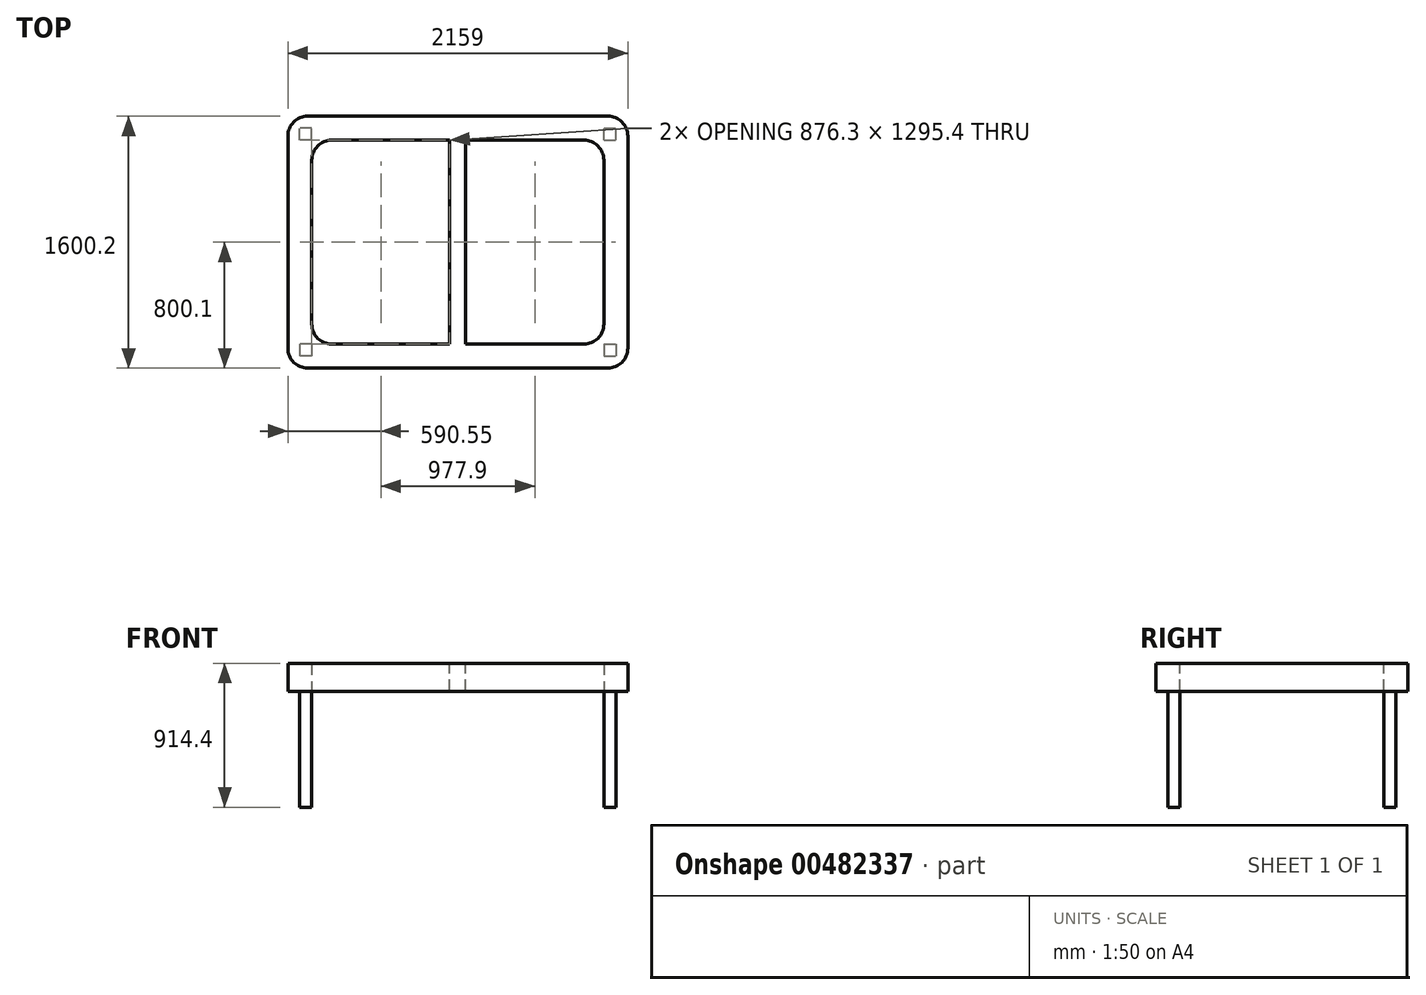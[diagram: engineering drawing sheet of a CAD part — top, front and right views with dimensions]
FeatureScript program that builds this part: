
annotation { "Feature Type Name" : "Feature", "Feature Type Description" : "" }
export const myFeature = defineFeature(function(context is Context, id is Id, definition is map)
    precondition{}
    {
        {
            var Q0;
            Q0=qCreatedBy(makeId("Top.planeOp"),FACE);
            var sketch = newSketch(context, id + "F0", { "sketchPlane" : qUnion([Q0])});
            skLineSegment(sketch, "E0.bottom", {"start": v(0, 0) * mm, "end": v(2159, 0) * mm});
            skLineSegment(sketch, "E0.top", {"start": v(0, 1600.2) * mm, "end": v(2159, 1600.2) * mm});
            skLineSegment(sketch, "E0.left", {"start": v(0, 0) * mm, "end": v(0, 1600.2) * mm});
            skLineSegment(sketch, "E0.right", {"start": v(2159, 0) * mm, "end": v(2159, 1600.2) * mm});
            skLineSegment(sketch, "E1.bottom", {"start": v(152.4, 152.4) * mm, "end": v(2006.6, 152.4) * mm});
            skLineSegment(sketch, "E1.top", {"start": v(152.4, 1447.8) * mm, "end": v(2006.6, 1447.8) * mm});
            skLineSegment(sketch, "E1.left", {"start": v(152.4, 152.4) * mm, "end": v(152.4, 1447.8) * mm});
            skLineSegment(sketch, "E1.right", {"start": v(2006.6, 152.4) * mm, "end": v(2006.6, 1447.8) * mm});
            skSolve(sketch);
        }
        {
            var Q0;
            Q0 = qSketchRegion(id + "F0", true);
            extrude(context, id + "F1", {"entities" : qUnion([Q0]), "depth" : 177.8 * mm, "offsetDistance" : 25.4 * mm});
        }
        {
            var Q0;
            Q0=makeQuery(id+"F1.opExtrude","CAP_FACE",FACE,{"disambiguationData":[OSD([sQuery(id+"F0.wireOp",EDGE,"E0.bottom"),sQuery(id+"F0.wireOp",EDGE,"E0.top"),sQuery(id+"F0.wireOp",EDGE,"E0.left"),sQuery(id+"F0.wireOp",EDGE,"E0.right"),sQuery(id+"F0.wireOp",EDGE,"E1.bottom"),sQuery(id+"F0.wireOp",EDGE,"E1.top"),sQuery(id+"F0.wireOp",EDGE,"E1.left"),sQuery(id+"F0.wireOp",EDGE,"E1.right")])],"isStart":true});
            var sketch = newSketch(context, id + "F2", { "sketchPlane" : qUnion([Q0])});
            skLineSegment(sketch, "E2.bottom", {"start": v(152.4, -152.4) * mm, "end": v(76.2, -152.4) * mm});
            skLineSegment(sketch, "E2.top", {"start": v(152.4, -76.2) * mm, "end": v(76.2, -76.2) * mm});
            skLineSegment(sketch, "E2.left", {"start": v(152.4, -152.4) * mm, "end": v(152.4, -76.2) * mm});
            skLineSegment(sketch, "E2.right", {"start": v(76.2, -152.4) * mm, "end": v(76.2, -76.2) * mm});
            skLineSegment(sketch, "E3.bottom", {"start": v(2006.6, -152.4) * mm, "end": v(2082.8, -152.4) * mm});
            skLineSegment(sketch, "E3.top", {"start": v(2006.6, -76.2) * mm, "end": v(2082.8, -76.2) * mm});
            skLineSegment(sketch, "E3.left", {"start": v(2006.6, -152.4) * mm, "end": v(2006.6, -76.2) * mm});
            skLineSegment(sketch, "E3.right", {"start": v(2082.8, -152.4) * mm, "end": v(2082.8, -76.2) * mm});
            skLineSegment(sketch, "E4.bottom", {"start": v(2006.6, -1447.8) * mm, "end": v(2082.8, -1447.8) * mm});
            skLineSegment(sketch, "E4.top", {"start": v(2006.6, -1524) * mm, "end": v(2082.8, -1524) * mm});
            skLineSegment(sketch, "E4.left", {"start": v(2006.6, -1447.8) * mm, "end": v(2006.6, -1524) * mm});
            skLineSegment(sketch, "E4.right", {"start": v(2082.8, -1447.8) * mm, "end": v(2082.8, -1524) * mm});
            skLineSegment(sketch, "E5.bottom", {"start": v(152.4, -1447.8) * mm, "end": v(76.2, -1447.8) * mm});
            skLineSegment(sketch, "E5.top", {"start": v(152.4, -1524) * mm, "end": v(76.2, -1524) * mm});
            skLineSegment(sketch, "E5.left", {"start": v(152.4, -1447.8) * mm, "end": v(152.4, -1524) * mm});
            skLineSegment(sketch, "E5.right", {"start": v(76.2, -1447.8) * mm, "end": v(76.2, -1524) * mm});
            skSolve(sketch);
        }
        {
            var Q0;
            Q0 = qSketchRegion(id + "F2", true);
            extrude(context, id + "F3", {"entities" : qUnion([Q0]), "operationType" : NewBodyOperationType.ADD, "depth" : 736.6 * mm, "offsetDistance" : 25.4 * mm});
        }
        {
            var Q0;
            Q0=makeQuery(id+"F1.opExtrude","SWEPT_EDGE",EDGE,{"disambiguationData":[OSD([sQuery(id+"F0.wireOp",EDGE,"E1.top"),sQuery(id+"F0.wireOp",EDGE,"E1.left")])]});
            var Q1;
            Q1=makeQuery(id+"F1.opExtrude","SWEPT_EDGE",EDGE,{"disambiguationData":[OSD([sQuery(id+"F0.wireOp",EDGE,"E1.top"),sQuery(id+"F0.wireOp",EDGE,"E1.right")])]});
            var Q2;
            Q2=makeQuery(id+"F1.opExtrude","SWEPT_EDGE",EDGE,{"disambiguationData":[OSD([sQuery(id+"F0.wireOp",EDGE,"E1.bottom"),sQuery(id+"F0.wireOp",EDGE,"E1.right")])]});
            var Q3;
            Q3=makeQuery(id+"F1.opExtrude","SWEPT_EDGE",EDGE,{"disambiguationData":[OSD([sQuery(id+"F0.wireOp",EDGE,"E1.bottom"),sQuery(id+"F0.wireOp",EDGE,"E1.left")])]});
            var Q4;
            Q4=makeQuery(id+"F1.opExtrude","SWEPT_EDGE",EDGE,{"disambiguationData":[OSD([sQuery(id+"F0.wireOp",EDGE,"E0.bottom"),sQuery(id+"F0.wireOp",EDGE,"E0.left")])]});
            var Q5;
            Q5=makeQuery(id+"F1.opExtrude","SWEPT_EDGE",EDGE,{"disambiguationData":[OSD([sQuery(id+"F0.wireOp",EDGE,"E0.top"),sQuery(id+"F0.wireOp",EDGE,"E0.left")])]});
            var Q6;
            Q6=makeQuery(id+"F1.opExtrude","SWEPT_EDGE",EDGE,{"disambiguationData":[OSD([sQuery(id+"F0.wireOp",EDGE,"E0.bottom"),sQuery(id+"F0.wireOp",EDGE,"E0.right")])]});
            var Q7;
            Q7=makeQuery(id+"F1.opExtrude","SWEPT_EDGE",EDGE,{"disambiguationData":[OSD([sQuery(id+"F0.wireOp",EDGE,"E0.top"),sQuery(id+"F0.wireOp",EDGE,"E0.right")])]});
            fillet(context, id + "F4", {"entities" : qUnion([Q0, Q1, Q2, Q3, Q4, Q5, Q6, Q7]), "radius" : 127 * mm, "tangentPropagation" : true, "allowEdgeOverflow" : false});
        }
        {
            var Q0;
            Q0=makeQuery(id+"F1.opExtrude","SWEPT_FACE",FACE,{"disambiguationData":[OSD([sQuery(id+"F0.wireOp",EDGE,"E1.bottom")])]});
            var sketch = newSketch(context, id + "F5", { "sketchPlane" : qUnion([Q0])});
            skLineSegment(sketch, "E6.bottom", {"start": v(-1028.7, 0) * mm, "end": v(-1130.3, 0) * mm});
            skLineSegment(sketch, "E6.top", {"start": v(-1028.7, 177.8) * mm, "end": v(-1130.3, 177.8) * mm});
            skLineSegment(sketch, "E6.left", {"start": v(-1028.7, 0) * mm, "end": v(-1028.7, 177.8) * mm});
            skLineSegment(sketch, "E6.right", {"start": v(-1130.3, 0) * mm, "end": v(-1130.3, 177.8) * mm});
            skSolve(sketch);
        }
        {
            var Q0;
            Q0 = qSketchRegion(id + "F5", true);
            extrude(context, id + "F6", {"entities" : qUnion([Q0]), "operationType" : NewBodyOperationType.ADD, "endBound" : BoundingType.UP_TO_NEXT, "depth" : 25.4 * mm, "offsetDistance" : 25.4 * mm});
        }
    });
